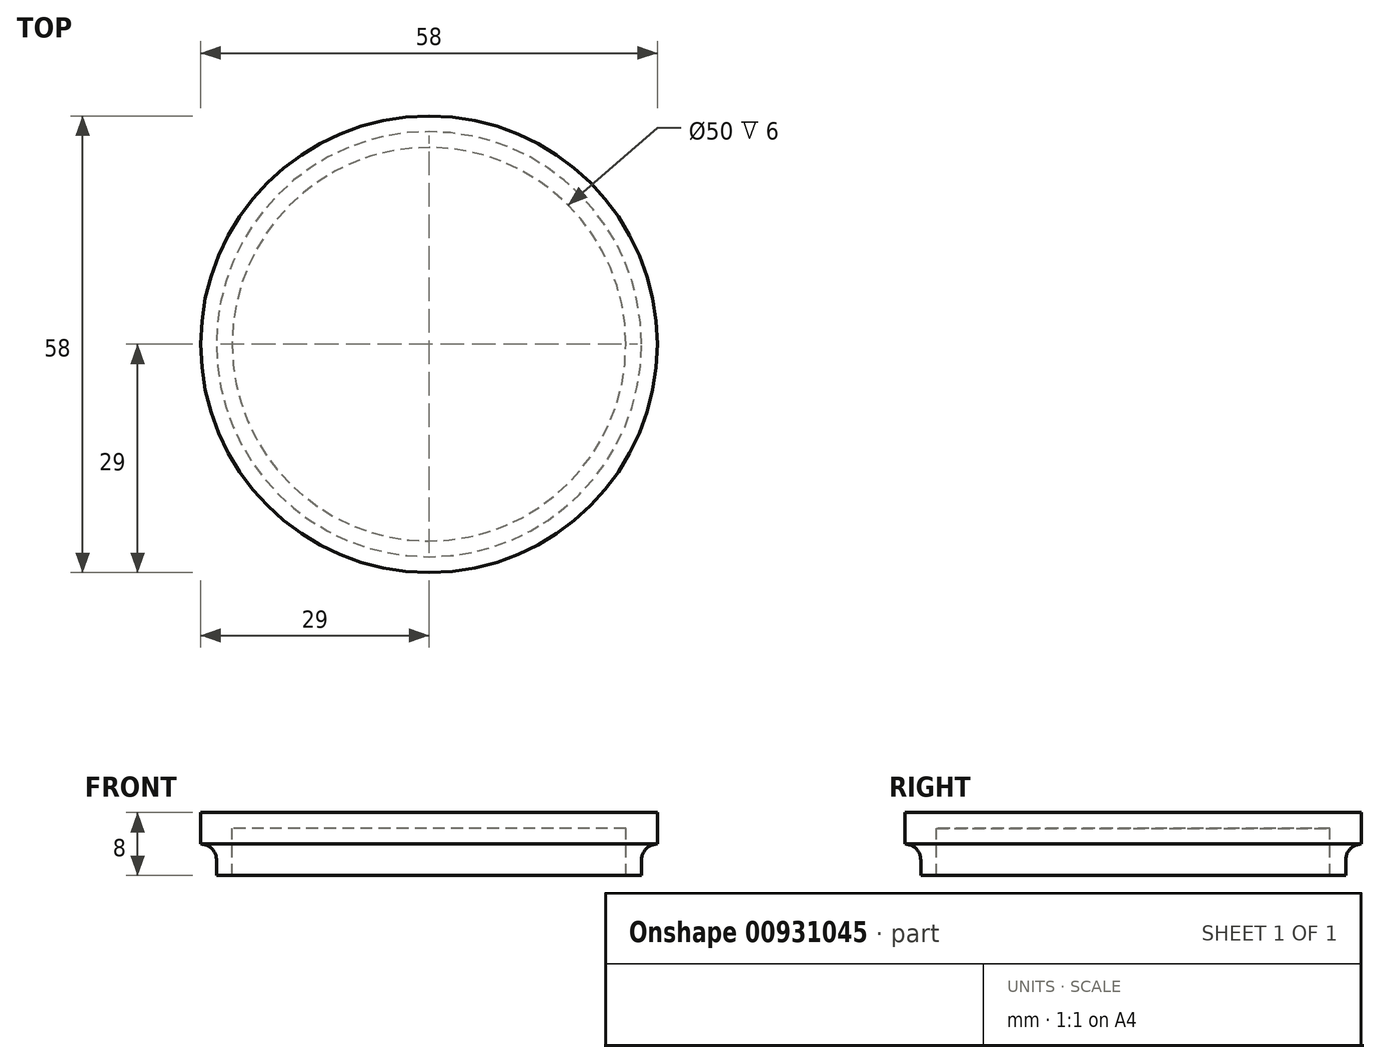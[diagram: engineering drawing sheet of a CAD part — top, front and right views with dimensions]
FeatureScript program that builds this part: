
annotation { "Feature Type Name" : "Feature", "Feature Type Description" : "" }
export const myFeature = defineFeature(function(context is Context, id is Id, definition is map)
    precondition{}
    {
        {
            var Q0;
            Q0=qCreatedBy(makeId("Right.planeOp"),FACE);
            var sketch = newSketch(context, id + "F0", { "sketchPlane" : qUnion([Q0])});
            skLineSegment(sketch, "E0.bottom", {"start": v(-25, -8) * mm, "end": v(-27, -8) * mm});
            skLineSegment(sketch, "E0.top", {"start": v(-25, -4) * mm, "end": v(-27, -4) * mm});
            skLineSegment(sketch, "E0.left", {"start": v(-25, -8) * mm, "end": v(-25, -4) * mm});
            skLineSegment(sketch, "E0.right", {"start": v(-27, -8) * mm, "end": v(-27, -4) * mm});
            skLineSegment(sketch, "E1.bottom", {"start": v(-25, -4) * mm, "end": v(-29, -4) * mm});
            skLineSegment(sketch, "E1.top", {"start": v(-25, 0) * mm, "end": v(-29, 0) * mm});
            skLineSegment(sketch, "E1.left", {"start": v(-25, -4) * mm, "end": v(-25, 0) * mm});
            skLineSegment(sketch, "E1.right", {"start": v(-29, -4) * mm, "end": v(-29, 0) * mm});
            skLineSegment(sketch, "E2.bottom", {"start": v(-25, 0) * mm, "end": v(0, 0) * mm});
            skLineSegment(sketch, "E2.top", {"start": v(-25, -2) * mm, "end": v(0, -2) * mm});
            skLineSegment(sketch, "E2.left", {"start": v(-25, 0) * mm, "end": v(-25, -2) * mm});
            skLineSegment(sketch, "E2.right", {"start": v(0, 0) * mm, "end": v(0, -2) * mm});
            skSolve(sketch);
        }
        {
            var Q0;
            Q0=makeQuery(id+"F0.imprint","IMPRINT",FACE,{"disambiguationData":[TD([[makeQuery(id+"F0.imprint","IMPRINT",EDGE,{"derivedFrom":sQuery(id+"F0.wireOp",EDGE,"E2.bottom")}),-1.0]])]});
            var Q1;
            Q1=makeQuery(id+"F0.imprint","IMPRINT",FACE,{"disambiguationData":[TD([[makeQuery(id+"F0.imprint","IMPRINT",EDGE,{"derivedFrom":sQuery(id+"F0.wireOp",EDGE,"E1.top")}),1.0]])]});
            var Q2;
            Q2=makeQuery(id+"F0.imprint","IMPRINT",FACE,{"disambiguationData":[TD([[makeQuery(id+"F0.imprint","IMPRINT",EDGE,{"derivedFrom":sQuery(id+"F0.wireOp",EDGE,"E0.bottom")}),-1.0]])]});
            var Q3;
            Q3=sQuery(id+"F0.wireOp",EDGE,"E2.right");
            revolve(context, id + "F1", {"surfaceOperationType" : NewSurfaceOperationType.NEW, "entities" : qUnion([Q0, Q1, Q2]), "axis" : qUnion([Q3]), "revolveType" : RevolveType.FULL});
        }
        {
            var Q0;
            Q0=makeQuery(id+"F1.opRevolve","SWEPT_EDGE",EDGE,{"disambiguationData":[OSD([sQuery(id+"F0.wireOp",EDGE,"E0.right"),sQuery(id+"F0.wireOp",EDGE,"E1.bottom")])]});
            fillet(context, id + "F2", {"entities" : qUnion([Q0]), "radius" : 2 * mm, "tangentPropagation" : true, "allowEdgeOverflow" : false});
        }
    });
